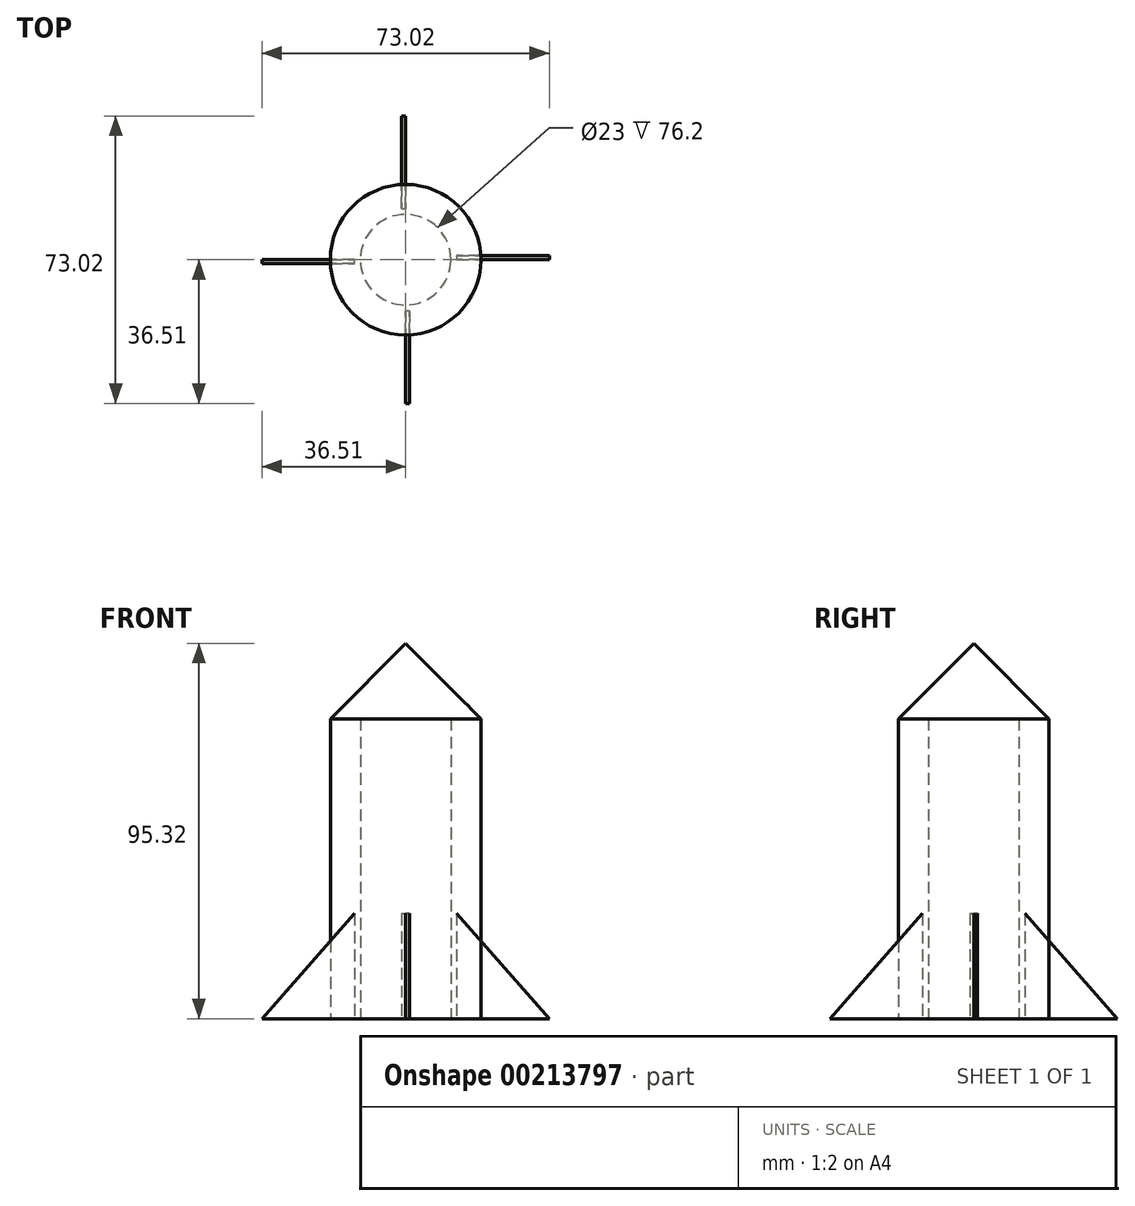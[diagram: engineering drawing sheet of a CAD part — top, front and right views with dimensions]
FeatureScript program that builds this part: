
annotation { "Feature Type Name" : "Feature", "Feature Type Description" : "" }
export const myFeature = defineFeature(function(context is Context, id is Id, definition is map)
    precondition{}
    {
        {
            var Q0;
            Q0=qCreatedBy(makeId("Top.planeOp"),FACE);
            var sketch = newSketch(context, id + "F0", { "sketchPlane" : qUnion([Q0])});
            skCircle(sketch, "E0", {"center": v(0, 0) * mm, "radius": 11.5 * mm});
            skCircle(sketch, "E1", {"center": v(0, 0) * mm, "radius": 19.12 * mm});
            skSolve(sketch);
        }
        {
            var Q0;
            Q0=makeQuery(id+"F0.imprint","IMPRINT",FACE,{"disambiguationData":[TD([[makeQuery(id+"F0.imprint","IMPRINT",EDGE,{"derivedFrom":sQuery(id+"F0.wireOp",EDGE,"E0")}),-1.0]])]});
            extrude(context, id + "F1", {"entities" : qUnion([Q0]), "depth" : 76.2 * mm});
        }
        {
            var Q0;
            Q0=makeQuery(id+"F1.opExtrude","CAP_FACE",FACE,{"disambiguationData":[OSD([sQuery(id+"F0.wireOp",EDGE,"E0"),sQuery(id+"F0.wireOp",EDGE,"E1")])],"isStart":false});
            var sketch = newSketch(context, id + "F2", { "sketchPlane" : qUnion([Q0])});
            skCircle(sketch, "E2.0", {"center": v(0, 0) * mm, "radius": 19.12 * mm});
            skSolve(sketch);
        }
        {
            var Q0;
            Q0=qSketchRegion(id+"F2",true);
            extrude(context, id + "F3", {"entities" : qUnion([Q0]), "operationType" : NewBodyOperationType.ADD, "depth" : 50.8 * mm, "hasDraft" : true, "draftAngle" : 45 * degree, "draftPullDirection" : true});
        }
        {
            var Q0;
            Q0=qCreatedBy(makeId("Right.planeOp"),FACE);
            var sketch = newSketch(context, id + "F4", { "sketchPlane" : qUnion([Q0])});
            skLineSegment(sketch, "E3", {"start": v(-13, 0) * mm, "end": v(-36.5, 0) * mm});
            skLineSegment(sketch, "E4", {"start": v(-36.5, 0) * mm, "end": v(-13, 26.76) * mm});
            skLineSegment(sketch, "E5", {"start": v(-13, 26.76) * mm, "end": v(-13, 0) * mm});
            skSolve(sketch);
        }
        {
            var Q0;
            Q0=makeQuery(id+"F4.imprint","IMPRINT",FACE,{"disambiguationData":[TD([[makeQuery(id+"F4.imprint","IMPRINT",EDGE,{"derivedFrom":sQuery(id+"F4.wireOp",EDGE,"E3")}),-1.0]])]});
            extrude(context, id + "F5", {"entities" : qUnion([Q0]), "depth" : 1 * mm});
        }
        {
            var Q0;
            Q0=makeQuery(id+"F5.opExtrude","SWEPT_BODY",BODY,{"disambiguationData":[OSD([sQuery(id+"F4.wireOp",EDGE,"E3"),sQuery(id+"F4.wireOp",EDGE,"E4"),sQuery(id+"F4.wireOp",EDGE,"E5")])]});
            var Q1;
            Q1=sQuery(id+"F0.wireOp",EDGE,"E0");
            circularPattern(context, id + "F6", {"entities" : qUnion([Q0]), "axis" : qUnion([Q1]), "angle" : 360 * degree, "instanceCount" : 4, "equalSpace" : true});
        }
    });
